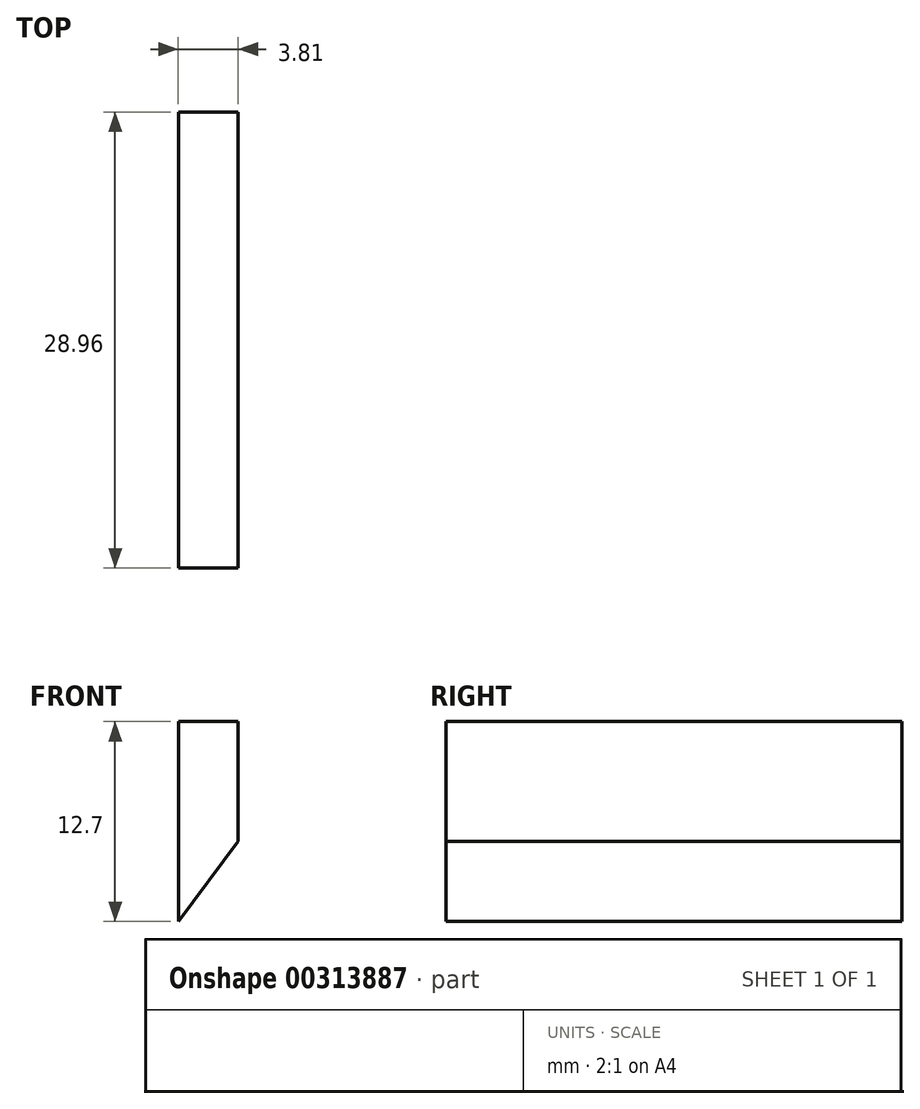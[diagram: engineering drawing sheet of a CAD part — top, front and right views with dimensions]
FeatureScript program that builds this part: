
annotation { "Feature Type Name" : "Feature", "Feature Type Description" : "" }
export const myFeature = defineFeature(function(context is Context, id is Id, definition is map)
    precondition{}
    {
        {
            var Q0;
            Q0=qCreatedBy(makeId("Front.planeOp"),FACE);
            var sketch = newSketch(context, id + "F0", { "sketchPlane" : qUnion([Q0])});
            skLineSegment(sketch, "E0", {"start": v(-52.95, 3) * mm, "end": v(-49.14, 3) * mm});
            skLineSegment(sketch, "E1", {"start": v(-49.14, 3) * mm, "end": v(-49.14, -4.63) * mm});
            skLineSegment(sketch, "E2", {"start": v(-52.95, 3) * mm, "end": v(-52.95, -9.7) * mm});
            skLineSegment(sketch, "E3", {"start": v(-52.95, -9.7) * mm, "end": v(-49.14, -4.63) * mm});
            skSolve(sketch);
        }
        {
            var Q0;
            Q0 = qSketchRegion(id + "F0", true);
            extrude(context, id + "F1", {"entities" : qUnion([Q0]), "depth" : 28.96 * mm});
        }
    });
